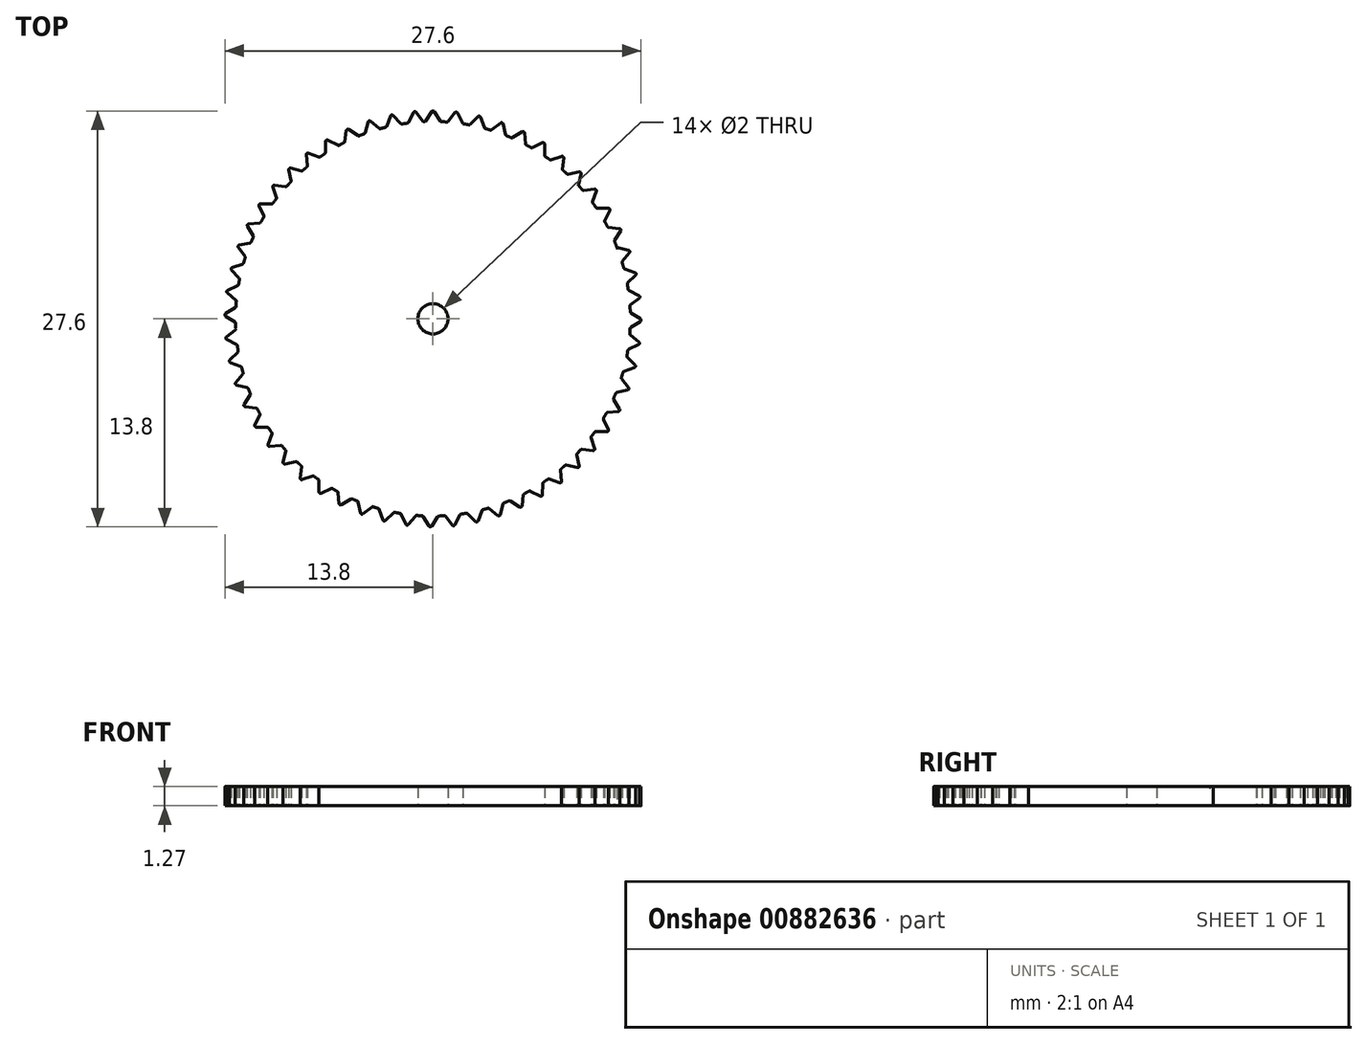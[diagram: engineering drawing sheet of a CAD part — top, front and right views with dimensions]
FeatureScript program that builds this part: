
annotation { "Feature Type Name" : "Feature", "Feature Type Description" : "" }
export const myFeature = defineFeature(function(context is Context, id is Id, definition is map)
    precondition{}
    {
        {
            var Q0;
            Q0=qCreatedBy(makeId("Top.planeOp"),FACE);
            var sketch = newSketch(context, id + "F0", { "sketchPlane" : qUnion([Q0])});
            skArc(sketch, "E0", {"start": v(-0.5, 13.09) * mm, "mid": v(0, -13.1) * mm, "end": v(0.5, 13.09) * mm});
            skLineSegment(sketch, "E1", {"start": v(-0.5, 13.09) * mm, "end": v(0, 13.9) * mm});
            skLineSegment(sketch, "E2", {"start": v(0, 13.9) * mm, "end": v(0.5, 13.09) * mm});
            skCircle(sketch, "E3", {"center": v(0, 0) * mm, "radius": 1 * mm});
            skLineSegment(sketch, "E4", {"start": v(-0.5, 13.09) * mm, "end": v(0.5, 13.09) * mm});
            skLineSegment(sketch, "E5.1.0", {"start": v(0.97, 13.06) * mm, "end": v(1.56, 13.8) * mm});
            skLineSegment(sketch, "E5.1.1", {"start": v(1.56, 13.8) * mm, "end": v(1.98, 12.95) * mm});
            skLineSegment(sketch, "E5.2.0", {"start": v(2.43, 12.87) * mm, "end": v(3.1, 13.54) * mm});
            skLineSegment(sketch, "E5.2.1", {"start": v(3.1, 13.54) * mm, "end": v(3.42, 12.64) * mm});
            skLineSegment(sketch, "E5.3.0", {"start": v(3.86, 12.52) * mm, "end": v(4.6, 13.1) * mm});
            skLineSegment(sketch, "E5.3.1", {"start": v(4.6, 13.1) * mm, "end": v(4.82, 12.18) * mm});
            skLineSegment(sketch, "E5.4.0", {"start": v(5.24, 12) * mm, "end": v(6.05, 12.5) * mm});
            skLineSegment(sketch, "E5.4.1", {"start": v(6.05, 12.5) * mm, "end": v(6.16, 11.56) * mm});
            skLineSegment(sketch, "E5.5.0", {"start": v(6.56, 11.34) * mm, "end": v(7.42, 11.75) * mm});
            skLineSegment(sketch, "E5.5.1", {"start": v(7.42, 11.75) * mm, "end": v(7.42, 10.8) * mm});
            skLineSegment(sketch, "E5.6.0", {"start": v(7.8, 10.53) * mm, "end": v(8.7, 10.84) * mm});
            skLineSegment(sketch, "E5.6.1", {"start": v(8.7, 10.84) * mm, "end": v(8.58, 9.9) * mm});
            skLineSegment(sketch, "E5.7.0", {"start": v(8.93, 9.58) * mm, "end": v(9.85, 9.8) * mm});
            skLineSegment(sketch, "E5.7.1", {"start": v(9.85, 9.8) * mm, "end": v(9.64, 8.86) * mm});
            skLineSegment(sketch, "E5.8.0", {"start": v(9.95, 8.52) * mm, "end": v(10.9, 8.62) * mm});
            skLineSegment(sketch, "E5.8.1", {"start": v(10.9, 8.62) * mm, "end": v(10.58, 7.72) * mm});
            skLineSegment(sketch, "E5.9.0", {"start": v(10.84, 7.35) * mm, "end": v(11.8, 7.34) * mm});
            skLineSegment(sketch, "E5.9.1", {"start": v(11.8, 7.34) * mm, "end": v(11.38, 6.49) * mm});
            skLineSegment(sketch, "E5.10.0", {"start": v(11.6, 6.08) * mm, "end": v(12.54, 5.97) * mm});
            skLineSegment(sketch, "E5.10.1", {"start": v(12.54, 5.97) * mm, "end": v(12.03, 5.17) * mm});
            skLineSegment(sketch, "E5.11.0", {"start": v(12.2, 4.74) * mm, "end": v(13.13, 4.52) * mm});
            skLineSegment(sketch, "E5.11.1", {"start": v(13.13, 4.52) * mm, "end": v(12.54, 3.78) * mm});
            skLineSegment(sketch, "E5.12.0", {"start": v(12.66, 3.34) * mm, "end": v(13.56, 3.02) * mm});
            skLineSegment(sketch, "E5.12.1", {"start": v(13.56, 3.02) * mm, "end": v(12.88, 2.35) * mm});
            skLineSegment(sketch, "E5.13.0", {"start": v(12.96, 1.9) * mm, "end": v(13.81, 1.47) * mm});
            skLineSegment(sketch, "E5.13.1", {"start": v(13.81, 1.47) * mm, "end": v(13.07, 0.88) * mm});
            skLineSegment(sketch, "E5.14.0", {"start": v(13.09, 0.42) * mm, "end": v(13.9, -0.09) * mm});
            skLineSegment(sketch, "E5.14.1", {"start": v(13.9, -0.09) * mm, "end": v(13.08, -0.6) * mm});
            skLineSegment(sketch, "E5.15.0", {"start": v(13.05, -1.05) * mm, "end": v(13.8, -1.65) * mm});
            skLineSegment(sketch, "E5.15.1", {"start": v(13.8, -1.65) * mm, "end": v(12.93, -2.06) * mm});
            skLineSegment(sketch, "E5.16.0", {"start": v(12.85, -2.51) * mm, "end": v(13.52, -3.19) * mm});
            skLineSegment(sketch, "E5.16.1", {"start": v(13.52, -3.19) * mm, "end": v(12.62, -3.5) * mm});
            skLineSegment(sketch, "E5.17.0", {"start": v(12.5, -3.94) * mm, "end": v(13.08, -4.69) * mm});
            skLineSegment(sketch, "E5.17.1", {"start": v(13.08, -4.69) * mm, "end": v(12.15, -4.9) * mm});
            skLineSegment(sketch, "E5.18.0", {"start": v(11.97, -5.32) * mm, "end": v(12.47, -6.13) * mm});
            skLineSegment(sketch, "E5.18.1", {"start": v(12.47, -6.13) * mm, "end": v(11.52, -6.23) * mm});
            skLineSegment(sketch, "E5.19.0", {"start": v(11.3, -6.63) * mm, "end": v(11.7, -7.5) * mm});
            skLineSegment(sketch, "E5.19.1", {"start": v(11.7, -7.5) * mm, "end": v(10.75, -7.49) * mm});
            skLineSegment(sketch, "E5.20.0", {"start": v(10.48, -7.86) * mm, "end": v(10.78, -8.76) * mm});
            skLineSegment(sketch, "E5.20.1", {"start": v(10.78, -8.76) * mm, "end": v(9.84, -8.65) * mm});
            skLineSegment(sketch, "E5.21.0", {"start": v(9.53, -8.99) * mm, "end": v(9.73, -9.92) * mm});
            skLineSegment(sketch, "E5.21.1", {"start": v(9.73, -9.92) * mm, "end": v(8.8, -9.7) * mm});
            skLineSegment(sketch, "E5.22.0", {"start": v(8.46, -10) * mm, "end": v(8.55, -10.95) * mm});
            skLineSegment(sketch, "E5.22.1", {"start": v(8.55, -10.95) * mm, "end": v(7.66, -10.63) * mm});
            skLineSegment(sketch, "E5.23.0", {"start": v(7.28, -10.89) * mm, "end": v(7.27, -11.84) * mm});
            skLineSegment(sketch, "E5.23.1", {"start": v(7.27, -11.84) * mm, "end": v(6.41, -11.42) * mm});
            skLineSegment(sketch, "E5.24.0", {"start": v(6, -11.64) * mm, "end": v(5.9, -12.58) * mm});
            skLineSegment(sketch, "E5.24.1", {"start": v(5.9, -12.58) * mm, "end": v(5.09, -12.07) * mm});
            skLineSegment(sketch, "E5.25.0", {"start": v(4.66, -12.24) * mm, "end": v(4.44, -13.16) * mm});
            skLineSegment(sketch, "E5.25.1", {"start": v(4.44, -13.16) * mm, "end": v(3.7, -12.56) * mm});
            skLineSegment(sketch, "E5.26.0", {"start": v(3.26, -12.69) * mm, "end": v(2.93, -13.58) * mm});
            skLineSegment(sketch, "E5.26.1", {"start": v(2.93, -13.58) * mm, "end": v(2.26, -12.9) * mm});
            skLineSegment(sketch, "E5.27.0", {"start": v(1.81, -12.97) * mm, "end": v(1.39, -13.82) * mm});
            skLineSegment(sketch, "E5.27.1", {"start": v(1.39, -13.82) * mm, "end": v(0.8, -13.07) * mm});
            skLineSegment(sketch, "E5.28.0", {"start": v(0.34, -13.1) * mm, "end": v(-0.18, -13.9) * mm});
            skLineSegment(sketch, "E5.28.1", {"start": v(-0.18, -13.9) * mm, "end": v(-0.67, -13.08) * mm});
            skLineSegment(sketch, "E5.29.0", {"start": v(-1.13, -13.05) * mm, "end": v(-1.74, -13.78) * mm});
            skLineSegment(sketch, "E5.29.1", {"start": v(-1.74, -13.78) * mm, "end": v(-2.14, -12.92) * mm});
            skLineSegment(sketch, "E5.30.0", {"start": v(-2.6, -12.84) * mm, "end": v(-3.28, -13.5) * mm});
            skLineSegment(sketch, "E5.30.1", {"start": v(-3.28, -13.5) * mm, "end": v(-3.58, -12.6) * mm});
            skLineSegment(sketch, "E5.31.0", {"start": v(-4.02, -12.47) * mm, "end": v(-4.77, -13.05) * mm});
            skLineSegment(sketch, "E5.31.1", {"start": v(-4.77, -13.05) * mm, "end": v(-4.97, -12.12) * mm});
            skLineSegment(sketch, "E5.32.0", {"start": v(-5.4, -11.93) * mm, "end": v(-6.2, -12.43) * mm});
            skLineSegment(sketch, "E5.32.1", {"start": v(-6.2, -12.43) * mm, "end": v(-6.3, -11.48) * mm});
            skLineSegment(sketch, "E5.33.0", {"start": v(-6.7, -11.25) * mm, "end": v(-7.57, -11.65) * mm});
            skLineSegment(sketch, "E5.33.1", {"start": v(-7.57, -11.65) * mm, "end": v(-7.55, -10.7) * mm});
            skLineSegment(sketch, "E5.34.0", {"start": v(-7.92, -10.43) * mm, "end": v(-8.83, -10.73) * mm});
            skLineSegment(sketch, "E5.34.1", {"start": v(-8.83, -10.73) * mm, "end": v(-8.7, -9.78) * mm});
            skLineSegment(sketch, "E5.35.0", {"start": v(-9.05, -9.47) * mm, "end": v(-9.98, -9.67) * mm});
            skLineSegment(sketch, "E5.35.1", {"start": v(-9.98, -9.67) * mm, "end": v(-9.75, -8.74) * mm});
            skLineSegment(sketch, "E5.36.0", {"start": v(-10.05, -8.4) * mm, "end": v(-11, -8.48) * mm});
            skLineSegment(sketch, "E5.36.1", {"start": v(-11, -8.48) * mm, "end": v(-10.67, -7.59) * mm});
            skLineSegment(sketch, "E5.37.0", {"start": v(-10.93, -7.21) * mm, "end": v(-11.88, -7.2) * mm});
            skLineSegment(sketch, "E5.37.1", {"start": v(-11.88, -7.2) * mm, "end": v(-11.46, -6.34) * mm});
            skLineSegment(sketch, "E5.38.0", {"start": v(-11.67, -5.94) * mm, "end": v(-12.62, -5.81) * mm});
            skLineSegment(sketch, "E5.38.1", {"start": v(-12.62, -5.81) * mm, "end": v(-12.1, -5.01) * mm});
            skLineSegment(sketch, "E5.39.0", {"start": v(-12.27, -4.59) * mm, "end": v(-13.2, -4.36) * mm});
            skLineSegment(sketch, "E5.39.1", {"start": v(-13.2, -4.36) * mm, "end": v(-12.59, -3.62) * mm});
            skLineSegment(sketch, "E5.40.0", {"start": v(-12.7, -3.18) * mm, "end": v(-13.6, -2.85) * mm});
            skLineSegment(sketch, "E5.40.1", {"start": v(-13.6, -2.85) * mm, "end": v(-12.91, -2.18) * mm});
            skLineSegment(sketch, "E5.41.0", {"start": v(-12.98, -1.73) * mm, "end": v(-13.83, -1.3) * mm});
            skLineSegment(sketch, "E5.41.1", {"start": v(-13.83, -1.3) * mm, "end": v(-13.08, -0.72) * mm});
            skLineSegment(sketch, "E5.42.0", {"start": v(-13.1, -0.26) * mm, "end": v(-13.89, 0.26) * mm});
            skLineSegment(sketch, "E5.42.1", {"start": v(-13.89, 0.26) * mm, "end": v(-13.07, 0.76) * mm});
            skLineSegment(sketch, "E5.43.0", {"start": v(-13.04, 1.21) * mm, "end": v(-13.77, 1.82) * mm});
            skLineSegment(sketch, "E5.43.1", {"start": v(-13.77, 1.82) * mm, "end": v(-12.9, 2.22) * mm});
            skLineSegment(sketch, "E5.44.0", {"start": v(-12.82, 2.67) * mm, "end": v(-13.48, 3.36) * mm});
            skLineSegment(sketch, "E5.44.1", {"start": v(-13.48, 3.36) * mm, "end": v(-12.58, 3.66) * mm});
            skLineSegment(sketch, "E5.45.0", {"start": v(-12.44, 4.1) * mm, "end": v(-13.02, 4.85) * mm});
            skLineSegment(sketch, "E5.45.1", {"start": v(-13.02, 4.85) * mm, "end": v(-12.08, 5.05) * mm});
            skLineSegment(sketch, "E5.46.0", {"start": v(-11.9, 5.47) * mm, "end": v(-12.39, 6.29) * mm});
            skLineSegment(sketch, "E5.46.1", {"start": v(-12.39, 6.29) * mm, "end": v(-11.44, 6.38) * mm});
            skLineSegment(sketch, "E5.47.0", {"start": v(-11.2, 6.77) * mm, "end": v(-11.6, 7.64) * mm});
            skLineSegment(sketch, "E5.47.1", {"start": v(-11.6, 7.64) * mm, "end": v(-10.65, 7.62) * mm});
            skLineSegment(sketch, "E5.48.0", {"start": v(-10.38, 8) * mm, "end": v(-10.67, 8.9) * mm});
            skLineSegment(sketch, "E5.48.1", {"start": v(-10.67, 8.9) * mm, "end": v(-9.73, 8.77) * mm});
            skLineSegment(sketch, "E5.49.0", {"start": v(-9.41, 9.1) * mm, "end": v(-9.6, 10.04) * mm});
            skLineSegment(sketch, "E5.49.1", {"start": v(-9.6, 10.04) * mm, "end": v(-8.68, 9.8) * mm});
            skLineSegment(sketch, "E5.50.0", {"start": v(-8.33, 10.1) * mm, "end": v(-8.41, 11.05) * mm});
            skLineSegment(sketch, "E5.50.1", {"start": v(-8.41, 11.05) * mm, "end": v(-7.52, 10.72) * mm});
            skLineSegment(sketch, "E5.51.0", {"start": v(-7.14, 10.98) * mm, "end": v(-7.12, 11.93) * mm});
            skLineSegment(sketch, "E5.51.1", {"start": v(-7.12, 11.93) * mm, "end": v(-6.27, 11.5) * mm});
            skLineSegment(sketch, "E5.52.0", {"start": v(-5.86, 11.71) * mm, "end": v(-5.73, 12.65) * mm});
            skLineSegment(sketch, "E5.52.1", {"start": v(-5.73, 12.65) * mm, "end": v(-4.94, 12.13) * mm});
            skLineSegment(sketch, "E5.53.0", {"start": v(-4.5, 12.3) * mm, "end": v(-4.27, 13.22) * mm});
            skLineSegment(sketch, "E5.53.1", {"start": v(-4.27, 13.22) * mm, "end": v(-3.54, 12.6) * mm});
            skLineSegment(sketch, "E5.54.0", {"start": v(-3.1, 12.73) * mm, "end": v(-2.76, 13.61) * mm});
            skLineSegment(sketch, "E5.54.1", {"start": v(-2.76, 13.61) * mm, "end": v(-2.1, 12.93) * mm});
            skLineSegment(sketch, "E5.55.0", {"start": v(-1.65, 13) * mm, "end": v(-1.21, 13.84) * mm});
            skLineSegment(sketch, "E5.55.1", {"start": v(-1.21, 13.84) * mm, "end": v(-0.63, 13.08) * mm});
            skLineSegment(sketch, "E5.anchor1", {"start": v(0, 0) * mm, "end": v(-0.5, 13.09) * mm, "construction": true});
            skLineSegment(sketch, "E5.anchor2", {"start": v(0, 0) * mm, "end": v(-1.65, 13) * mm, "construction": true});
            skSolve(sketch);
        }
        {
            var Q0;
            {var subQ0=sQuery(id+"F0.wireOp",EDGE,"E0");var subQ1=makeQuery(id+"F0.imprint","INTERSECT",VERTEX,{"derivedFrom":[subQ0,sQuery(id+"F0.wireOp",EDGE,"E2")]});Q0=makeQuery(id+"F0.imprint","IMPRINT",FACE,{"disambiguationData":[TD([[makeQuery(id+"F0.imprint","IMPRINT",EDGE,{"disambiguationData":[TD([[subQ1,-1.0]])],"derivedFrom":subQ0}),1.0]])]});}
            var Q1;
            {var subQ0=sQuery(id+"F0.wireOp",EDGE,"E2");Q1=makeQuery(id+"F0.imprint","IMPRINT",FACE,{"disambiguationData":[TD([[makeQuery(id+"F0.imprint","IMPRINT",EDGE,{"derivedFrom":subQ0}),-1.0]])]});}
            var Q2;
            {var subQ0=sQuery(id+"F0.wireOp",EDGE,"E1");Q2=makeQuery(id+"F0.imprint","IMPRINT",FACE,{"disambiguationData":[TD([[makeQuery(id+"F0.imprint","IMPRINT",EDGE,{"derivedFrom":subQ0}),-1.0]])]});}
            var Q3;
            {var subQ0=sQuery(id+"F0.wireOp",EDGE,"E5.55.0");Q3=makeQuery(id+"F0.imprint","IMPRINT",FACE,{"disambiguationData":[TD([[makeQuery(id+"F0.imprint","IMPRINT",EDGE,{"derivedFrom":subQ0}),-1.0]])]});}
            var Q4;
            {var subQ0=sQuery(id+"F0.wireOp",EDGE,"E5.54.0");Q4=makeQuery(id+"F0.imprint","IMPRINT",FACE,{"disambiguationData":[TD([[makeQuery(id+"F0.imprint","IMPRINT",EDGE,{"derivedFrom":subQ0}),-1.0]])]});}
            var Q5;
            {var subQ0=sQuery(id+"F0.wireOp",EDGE,"E5.53.0");Q5=makeQuery(id+"F0.imprint","IMPRINT",FACE,{"disambiguationData":[TD([[makeQuery(id+"F0.imprint","IMPRINT",EDGE,{"derivedFrom":subQ0}),-1.0]])]});}
            var Q6;
            {var subQ0=sQuery(id+"F0.wireOp",EDGE,"E5.52.0");Q6=makeQuery(id+"F0.imprint","IMPRINT",FACE,{"disambiguationData":[TD([[makeQuery(id+"F0.imprint","IMPRINT",EDGE,{"derivedFrom":subQ0}),-1.0]])]});}
            var Q7;
            {var subQ0=sQuery(id+"F0.wireOp",EDGE,"E5.51.0");Q7=makeQuery(id+"F0.imprint","IMPRINT",FACE,{"disambiguationData":[TD([[makeQuery(id+"F0.imprint","IMPRINT",EDGE,{"derivedFrom":subQ0}),-1.0]])]});}
            var Q8;
            {var subQ0=sQuery(id+"F0.wireOp",EDGE,"E5.50.0");Q8=makeQuery(id+"F0.imprint","IMPRINT",FACE,{"disambiguationData":[TD([[makeQuery(id+"F0.imprint","IMPRINT",EDGE,{"derivedFrom":subQ0}),-1.0]])]});}
            var Q9;
            {var subQ0=sQuery(id+"F0.wireOp",EDGE,"E5.49.0");Q9=makeQuery(id+"F0.imprint","IMPRINT",FACE,{"disambiguationData":[TD([[makeQuery(id+"F0.imprint","IMPRINT",EDGE,{"derivedFrom":subQ0}),-1.0]])]});}
            var Q10;
            {var subQ0=sQuery(id+"F0.wireOp",EDGE,"E5.48.0");Q10=makeQuery(id+"F0.imprint","IMPRINT",FACE,{"disambiguationData":[TD([[makeQuery(id+"F0.imprint","IMPRINT",EDGE,{"derivedFrom":subQ0}),-1.0]])]});}
            var Q11;
            {var subQ0=sQuery(id+"F0.wireOp",EDGE,"E5.47.0");Q11=makeQuery(id+"F0.imprint","IMPRINT",FACE,{"disambiguationData":[TD([[makeQuery(id+"F0.imprint","IMPRINT",EDGE,{"derivedFrom":subQ0}),-1.0]])]});}
            var Q12;
            {var subQ0=sQuery(id+"F0.wireOp",EDGE,"E5.46.0");Q12=makeQuery(id+"F0.imprint","IMPRINT",FACE,{"disambiguationData":[TD([[makeQuery(id+"F0.imprint","IMPRINT",EDGE,{"derivedFrom":subQ0}),-1.0]])]});}
            var Q13;
            {var subQ0=sQuery(id+"F0.wireOp",EDGE,"E5.45.0");Q13=makeQuery(id+"F0.imprint","IMPRINT",FACE,{"disambiguationData":[TD([[makeQuery(id+"F0.imprint","IMPRINT",EDGE,{"derivedFrom":subQ0}),-1.0]])]});}
            var Q14;
            {var subQ0=sQuery(id+"F0.wireOp",EDGE,"E5.44.0");Q14=makeQuery(id+"F0.imprint","IMPRINT",FACE,{"disambiguationData":[TD([[makeQuery(id+"F0.imprint","IMPRINT",EDGE,{"derivedFrom":subQ0}),-1.0]])]});}
            var Q15;
            {var subQ0=sQuery(id+"F0.wireOp",EDGE,"E5.42.0");Q15=makeQuery(id+"F0.imprint","IMPRINT",FACE,{"disambiguationData":[TD([[makeQuery(id+"F0.imprint","IMPRINT",EDGE,{"derivedFrom":subQ0}),-1.0]])]});}
            var Q16;
            {var subQ0=sQuery(id+"F0.wireOp",EDGE,"E5.43.0");Q16=makeQuery(id+"F0.imprint","IMPRINT",FACE,{"disambiguationData":[TD([[makeQuery(id+"F0.imprint","IMPRINT",EDGE,{"derivedFrom":subQ0}),-1.0]])]});}
            var Q17;
            {var subQ0=sQuery(id+"F0.wireOp",EDGE,"E5.41.0");Q17=makeQuery(id+"F0.imprint","IMPRINT",FACE,{"disambiguationData":[TD([[makeQuery(id+"F0.imprint","IMPRINT",EDGE,{"derivedFrom":subQ0}),-1.0]])]});}
            var Q18;
            {var subQ0=sQuery(id+"F0.wireOp",EDGE,"E5.40.0");Q18=makeQuery(id+"F0.imprint","IMPRINT",FACE,{"disambiguationData":[TD([[makeQuery(id+"F0.imprint","IMPRINT",EDGE,{"derivedFrom":subQ0}),-1.0]])]});}
            var Q19;
            {var subQ0=sQuery(id+"F0.wireOp",EDGE,"E5.39.0");Q19=makeQuery(id+"F0.imprint","IMPRINT",FACE,{"disambiguationData":[TD([[makeQuery(id+"F0.imprint","IMPRINT",EDGE,{"derivedFrom":subQ0}),-1.0]])]});}
            var Q20;
            {var subQ0=sQuery(id+"F0.wireOp",EDGE,"E5.38.0");Q20=makeQuery(id+"F0.imprint","IMPRINT",FACE,{"disambiguationData":[TD([[makeQuery(id+"F0.imprint","IMPRINT",EDGE,{"derivedFrom":subQ0}),-1.0]])]});}
            var Q21;
            {var subQ0=sQuery(id+"F0.wireOp",EDGE,"E5.37.0");Q21=makeQuery(id+"F0.imprint","IMPRINT",FACE,{"disambiguationData":[TD([[makeQuery(id+"F0.imprint","IMPRINT",EDGE,{"derivedFrom":subQ0}),-1.0]])]});}
            var Q22;
            {var subQ0=sQuery(id+"F0.wireOp",EDGE,"E5.36.0");Q22=makeQuery(id+"F0.imprint","IMPRINT",FACE,{"disambiguationData":[TD([[makeQuery(id+"F0.imprint","IMPRINT",EDGE,{"derivedFrom":subQ0}),-1.0]])]});}
            var Q23;
            {var subQ0=sQuery(id+"F0.wireOp",EDGE,"E5.35.0");Q23=makeQuery(id+"F0.imprint","IMPRINT",FACE,{"disambiguationData":[TD([[makeQuery(id+"F0.imprint","IMPRINT",EDGE,{"derivedFrom":subQ0}),-1.0]])]});}
            var Q24;
            {var subQ0=sQuery(id+"F0.wireOp",EDGE,"E5.34.0");Q24=makeQuery(id+"F0.imprint","IMPRINT",FACE,{"disambiguationData":[TD([[makeQuery(id+"F0.imprint","IMPRINT",EDGE,{"derivedFrom":subQ0}),-1.0]])]});}
            var Q25;
            {var subQ0=sQuery(id+"F0.wireOp",EDGE,"E5.33.0");Q25=makeQuery(id+"F0.imprint","IMPRINT",FACE,{"disambiguationData":[TD([[makeQuery(id+"F0.imprint","IMPRINT",EDGE,{"derivedFrom":subQ0}),-1.0]])]});}
            var Q26;
            {var subQ0=sQuery(id+"F0.wireOp",EDGE,"E5.32.0");Q26=makeQuery(id+"F0.imprint","IMPRINT",FACE,{"disambiguationData":[TD([[makeQuery(id+"F0.imprint","IMPRINT",EDGE,{"derivedFrom":subQ0}),-1.0]])]});}
            var Q27;
            {var subQ0=sQuery(id+"F0.wireOp",EDGE,"E5.31.0");Q27=makeQuery(id+"F0.imprint","IMPRINT",FACE,{"disambiguationData":[TD([[makeQuery(id+"F0.imprint","IMPRINT",EDGE,{"derivedFrom":subQ0}),-1.0]])]});}
            var Q28;
            {var subQ0=sQuery(id+"F0.wireOp",EDGE,"E5.30.0");Q28=makeQuery(id+"F0.imprint","IMPRINT",FACE,{"disambiguationData":[TD([[makeQuery(id+"F0.imprint","IMPRINT",EDGE,{"derivedFrom":subQ0}),-1.0]])]});}
            var Q29;
            {var subQ0=sQuery(id+"F0.wireOp",EDGE,"E5.29.0");Q29=makeQuery(id+"F0.imprint","IMPRINT",FACE,{"disambiguationData":[TD([[makeQuery(id+"F0.imprint","IMPRINT",EDGE,{"derivedFrom":subQ0}),-1.0]])]});}
            var Q30;
            {var subQ0=sQuery(id+"F0.wireOp",EDGE,"E5.28.0");Q30=makeQuery(id+"F0.imprint","IMPRINT",FACE,{"disambiguationData":[TD([[makeQuery(id+"F0.imprint","IMPRINT",EDGE,{"derivedFrom":subQ0}),-1.0]])]});}
            var Q31;
            {var subQ0=sQuery(id+"F0.wireOp",EDGE,"E5.27.0");Q31=makeQuery(id+"F0.imprint","IMPRINT",FACE,{"disambiguationData":[TD([[makeQuery(id+"F0.imprint","IMPRINT",EDGE,{"derivedFrom":subQ0}),-1.0]])]});}
            var Q32;
            {var subQ0=sQuery(id+"F0.wireOp",EDGE,"E5.26.0");Q32=makeQuery(id+"F0.imprint","IMPRINT",FACE,{"disambiguationData":[TD([[makeQuery(id+"F0.imprint","IMPRINT",EDGE,{"derivedFrom":subQ0}),-1.0]])]});}
            var Q33;
            {var subQ0=sQuery(id+"F0.wireOp",EDGE,"E5.25.0");Q33=makeQuery(id+"F0.imprint","IMPRINT",FACE,{"disambiguationData":[TD([[makeQuery(id+"F0.imprint","IMPRINT",EDGE,{"derivedFrom":subQ0}),-1.0]])]});}
            var Q34;
            {var subQ0=sQuery(id+"F0.wireOp",EDGE,"E5.24.0");Q34=makeQuery(id+"F0.imprint","IMPRINT",FACE,{"disambiguationData":[TD([[makeQuery(id+"F0.imprint","IMPRINT",EDGE,{"derivedFrom":subQ0}),-1.0]])]});}
            var Q35;
            {var subQ0=sQuery(id+"F0.wireOp",EDGE,"E5.23.0");Q35=makeQuery(id+"F0.imprint","IMPRINT",FACE,{"disambiguationData":[TD([[makeQuery(id+"F0.imprint","IMPRINT",EDGE,{"derivedFrom":subQ0}),-1.0]])]});}
            var Q36;
            {var subQ0=sQuery(id+"F0.wireOp",EDGE,"E5.21.0");Q36=makeQuery(id+"F0.imprint","IMPRINT",FACE,{"disambiguationData":[TD([[makeQuery(id+"F0.imprint","IMPRINT",EDGE,{"derivedFrom":subQ0}),-1.0]])]});}
            var Q37;
            {var subQ0=sQuery(id+"F0.wireOp",EDGE,"E5.20.0");Q37=makeQuery(id+"F0.imprint","IMPRINT",FACE,{"disambiguationData":[TD([[makeQuery(id+"F0.imprint","IMPRINT",EDGE,{"derivedFrom":subQ0}),-1.0]])]});}
            var Q38;
            {var subQ0=sQuery(id+"F0.wireOp",EDGE,"E5.19.0");Q38=makeQuery(id+"F0.imprint","IMPRINT",FACE,{"disambiguationData":[TD([[makeQuery(id+"F0.imprint","IMPRINT",EDGE,{"derivedFrom":subQ0}),-1.0]])]});}
            var Q39;
            {var subQ0=sQuery(id+"F0.wireOp",EDGE,"E5.18.0");Q39=makeQuery(id+"F0.imprint","IMPRINT",FACE,{"disambiguationData":[TD([[makeQuery(id+"F0.imprint","IMPRINT",EDGE,{"derivedFrom":subQ0}),-1.0]])]});}
            var Q40;
            {var subQ0=sQuery(id+"F0.wireOp",EDGE,"E5.22.0");Q40=makeQuery(id+"F0.imprint","IMPRINT",FACE,{"disambiguationData":[TD([[makeQuery(id+"F0.imprint","IMPRINT",EDGE,{"derivedFrom":subQ0}),-1.0]])]});}
            var Q41;
            {var subQ0=sQuery(id+"F0.wireOp",EDGE,"E5.17.0");Q41=makeQuery(id+"F0.imprint","IMPRINT",FACE,{"disambiguationData":[TD([[makeQuery(id+"F0.imprint","IMPRINT",EDGE,{"derivedFrom":subQ0}),-1.0]])]});}
            var Q42;
            {var subQ0=sQuery(id+"F0.wireOp",EDGE,"E5.16.0");Q42=makeQuery(id+"F0.imprint","IMPRINT",FACE,{"disambiguationData":[TD([[makeQuery(id+"F0.imprint","IMPRINT",EDGE,{"derivedFrom":subQ0}),-1.0]])]});}
            var Q43;
            {var subQ0=sQuery(id+"F0.wireOp",EDGE,"E5.14.0");Q43=makeQuery(id+"F0.imprint","IMPRINT",FACE,{"disambiguationData":[TD([[makeQuery(id+"F0.imprint","IMPRINT",EDGE,{"derivedFrom":subQ0}),-1.0]])]});}
            var Q44;
            {var subQ0=sQuery(id+"F0.wireOp",EDGE,"E5.15.0");Q44=makeQuery(id+"F0.imprint","IMPRINT",FACE,{"disambiguationData":[TD([[makeQuery(id+"F0.imprint","IMPRINT",EDGE,{"derivedFrom":subQ0}),-1.0]])]});}
            var Q45;
            Q45=makeQuery(id+"F0.imprint","IMPRINT",FACE,{"disambiguationData":[TD([[makeQuery(id+"F0.imprint","IMPRINT",EDGE,{"derivedFrom":sQuery(id+"F0.wireOp",EDGE,"E3")}),-1.0]])]});
            var Q46;
            {var subQ0=sQuery(id+"F0.wireOp",EDGE,"E5.13.0");Q46=makeQuery(id+"F0.imprint","IMPRINT",FACE,{"disambiguationData":[TD([[makeQuery(id+"F0.imprint","IMPRINT",EDGE,{"derivedFrom":subQ0}),-1.0]])]});}
            var Q47;
            {var subQ0=sQuery(id+"F0.wireOp",EDGE,"E5.12.0");Q47=makeQuery(id+"F0.imprint","IMPRINT",FACE,{"disambiguationData":[TD([[makeQuery(id+"F0.imprint","IMPRINT",EDGE,{"derivedFrom":subQ0}),-1.0]])]});}
            var Q48;
            {var subQ0=sQuery(id+"F0.wireOp",EDGE,"E5.11.0");Q48=makeQuery(id+"F0.imprint","IMPRINT",FACE,{"disambiguationData":[TD([[makeQuery(id+"F0.imprint","IMPRINT",EDGE,{"derivedFrom":subQ0}),-1.0]])]});}
            var Q49;
            {var subQ0=sQuery(id+"F0.wireOp",EDGE,"E5.8.0");Q49=makeQuery(id+"F0.imprint","IMPRINT",FACE,{"disambiguationData":[TD([[makeQuery(id+"F0.imprint","IMPRINT",EDGE,{"derivedFrom":subQ0}),-1.0]])]});}
            var Q50;
            {var subQ0=sQuery(id+"F0.wireOp",EDGE,"E5.7.0");Q50=makeQuery(id+"F0.imprint","IMPRINT",FACE,{"disambiguationData":[TD([[makeQuery(id+"F0.imprint","IMPRINT",EDGE,{"derivedFrom":subQ0}),-1.0]])]});}
            var Q51;
            {var subQ0=sQuery(id+"F0.wireOp",EDGE,"E5.6.0");Q51=makeQuery(id+"F0.imprint","IMPRINT",FACE,{"disambiguationData":[TD([[makeQuery(id+"F0.imprint","IMPRINT",EDGE,{"derivedFrom":subQ0}),-1.0]])]});}
            var Q52;
            {var subQ0=sQuery(id+"F0.wireOp",EDGE,"E5.10.0");Q52=makeQuery(id+"F0.imprint","IMPRINT",FACE,{"disambiguationData":[TD([[makeQuery(id+"F0.imprint","IMPRINT",EDGE,{"derivedFrom":subQ0}),-1.0]])]});}
            var Q53;
            {var subQ0=sQuery(id+"F0.wireOp",EDGE,"E5.9.0");Q53=makeQuery(id+"F0.imprint","IMPRINT",FACE,{"disambiguationData":[TD([[makeQuery(id+"F0.imprint","IMPRINT",EDGE,{"derivedFrom":subQ0}),-1.0]])]});}
            var Q54;
            {var subQ0=sQuery(id+"F0.wireOp",EDGE,"E5.5.0");Q54=makeQuery(id+"F0.imprint","IMPRINT",FACE,{"disambiguationData":[TD([[makeQuery(id+"F0.imprint","IMPRINT",EDGE,{"derivedFrom":subQ0}),-1.0]])]});}
            var Q55;
            {var subQ0=sQuery(id+"F0.wireOp",EDGE,"E5.3.0");Q55=makeQuery(id+"F0.imprint","IMPRINT",FACE,{"disambiguationData":[TD([[makeQuery(id+"F0.imprint","IMPRINT",EDGE,{"derivedFrom":subQ0}),-1.0]])]});}
            var Q56;
            {var subQ0=sQuery(id+"F0.wireOp",EDGE,"E5.2.0");Q56=makeQuery(id+"F0.imprint","IMPRINT",FACE,{"disambiguationData":[TD([[makeQuery(id+"F0.imprint","IMPRINT",EDGE,{"derivedFrom":subQ0}),-1.0]])]});}
            var Q57;
            {var subQ0=sQuery(id+"F0.wireOp",EDGE,"E5.1.0");Q57=makeQuery(id+"F0.imprint","IMPRINT",FACE,{"disambiguationData":[TD([[makeQuery(id+"F0.imprint","IMPRINT",EDGE,{"derivedFrom":subQ0}),-1.0]])]});}
            var Q58;
            {var subQ0=sQuery(id+"F0.wireOp",EDGE,"E5.4.0");Q58=makeQuery(id+"F0.imprint","IMPRINT",FACE,{"disambiguationData":[TD([[makeQuery(id+"F0.imprint","IMPRINT",EDGE,{"derivedFrom":subQ0}),-1.0]])]});}
            extrude(context, id + "F1", {"entities" : qUnion([Q0, Q1, Q2, Q3, Q4, Q5, Q6, Q7, Q8, Q9, Q10, Q11, Q12, Q13, Q14, Q15, Q16, Q17, Q18, Q19, Q20, Q21, Q22, Q23, Q24, Q25, Q26, Q27, Q28, Q29, Q30, Q31, Q32, Q33, Q34, Q35, Q36, Q37, Q38, Q39, Q40, Q41, Q42, Q43, Q44, Q45, Q46, Q47, Q48, Q49, Q50, Q51, Q52, Q53, Q54, Q55, Q56, Q57, Q58]), "depth" : 1.27 * mm, "offsetDistance" : 25.4 * mm});
        }
        {
            var Q0;
            Q0=makeQuery(id+"F1.opExtrude","SWEPT_EDGE",EDGE,{"disambiguationData":[OSD([sQuery(id+"F0.wireOp",EDGE,"hA7iAoV0-JRGM-B4cx-GfAK-cCa6ma2gju5E"),sQuery(id+"F0.wireOp",EDGE,"E1"),sQuery(id+"F0.wireOp",EDGE,"E2")])]});
            var Q1;
            Q1=makeQuery(id+"F1.opExtrude","SWEPT_EDGE",EDGE,{"disambiguationData":[OSD([sQuery(id+"F0.wireOp",EDGE,"E0"),sQuery(id+"F0.wireOp",EDGE,"E5.41.1")])]});
            var Q2;
            Q2=makeQuery(id+"F1.opExtrude","SWEPT_EDGE",EDGE,{"disambiguationData":[OSD([sQuery(id+"F0.wireOp",EDGE,"E0"),sQuery(id+"F0.wireOp",EDGE,"E5.42.0")])]});
            var Q3;
            Q3=makeQuery(id+"F1.opExtrude","SWEPT_EDGE",EDGE,{"disambiguationData":[OSD([sQuery(id+"F0.wireOp",EDGE,"E5.42.0"),sQuery(id+"F0.wireOp",EDGE,"E5.42.1")])]});
            var Q4;
            Q4=makeQuery(id+"F1.opExtrude","SWEPT_EDGE",EDGE,{"disambiguationData":[OSD([sQuery(id+"F0.wireOp",EDGE,"E0"),sQuery(id+"F0.wireOp",EDGE,"E5.42.1")])]});
            var Q5;
            Q5=makeQuery(id+"F1.opExtrude","SWEPT_EDGE",EDGE,{"disambiguationData":[OSD([sQuery(id+"F0.wireOp",EDGE,"E0"),sQuery(id+"F0.wireOp",EDGE,"E5.43.0")])]});
            var Q6;
            Q6=makeQuery(id+"F1.opExtrude","SWEPT_EDGE",EDGE,{"disambiguationData":[OSD([sQuery(id+"F0.wireOp",EDGE,"E5.43.0"),sQuery(id+"F0.wireOp",EDGE,"E5.43.1")])]});
            var Q7;
            Q7=makeQuery(id+"F1.opExtrude","SWEPT_EDGE",EDGE,{"disambiguationData":[OSD([sQuery(id+"F0.wireOp",EDGE,"E0"),sQuery(id+"F0.wireOp",EDGE,"E5.43.1")])]});
            var Q8;
            Q8=makeQuery(id+"F1.opExtrude","SWEPT_EDGE",EDGE,{"disambiguationData":[OSD([sQuery(id+"F0.wireOp",EDGE,"E0"),sQuery(id+"F0.wireOp",EDGE,"E5.44.0")])]});
            var Q9;
            Q9=makeQuery(id+"F1.opExtrude","SWEPT_EDGE",EDGE,{"disambiguationData":[OSD([sQuery(id+"F0.wireOp",EDGE,"E5.44.0"),sQuery(id+"F0.wireOp",EDGE,"E5.44.1")])]});
            var Q10;
            Q10=makeQuery(id+"F1.opExtrude","SWEPT_EDGE",EDGE,{"disambiguationData":[OSD([sQuery(id+"F0.wireOp",EDGE,"E0"),sQuery(id+"F0.wireOp",EDGE,"E5.44.1")])]});
            var Q11;
            Q11=makeQuery(id+"F1.opExtrude","SWEPT_EDGE",EDGE,{"disambiguationData":[OSD([sQuery(id+"F0.wireOp",EDGE,"E0"),sQuery(id+"F0.wireOp",EDGE,"E5.45.0")])]});
            var Q12;
            Q12=makeQuery(id+"F1.opExtrude","SWEPT_EDGE",EDGE,{"disambiguationData":[OSD([sQuery(id+"F0.wireOp",EDGE,"E5.45.0"),sQuery(id+"F0.wireOp",EDGE,"E5.45.1")])]});
            var Q13;
            Q13=makeQuery(id+"F1.opExtrude","SWEPT_EDGE",EDGE,{"disambiguationData":[OSD([sQuery(id+"F0.wireOp",EDGE,"E0"),sQuery(id+"F0.wireOp",EDGE,"E5.45.1")])]});
            var Q14;
            Q14=makeQuery(id+"F1.opExtrude","SWEPT_EDGE",EDGE,{"disambiguationData":[OSD([sQuery(id+"F0.wireOp",EDGE,"E0"),sQuery(id+"F0.wireOp",EDGE,"E5.46.0")])]});
            var Q15;
            Q15=makeQuery(id+"F1.opExtrude","SWEPT_EDGE",EDGE,{"disambiguationData":[OSD([sQuery(id+"F0.wireOp",EDGE,"E5.46.0"),sQuery(id+"F0.wireOp",EDGE,"E5.46.1")])]});
            var Q16;
            Q16=makeQuery(id+"F1.opExtrude","SWEPT_EDGE",EDGE,{"disambiguationData":[OSD([sQuery(id+"F0.wireOp",EDGE,"E0"),sQuery(id+"F0.wireOp",EDGE,"E5.46.1")])]});
            var Q17;
            Q17=makeQuery(id+"F1.opExtrude","SWEPT_EDGE",EDGE,{"disambiguationData":[OSD([sQuery(id+"F0.wireOp",EDGE,"E0"),sQuery(id+"F0.wireOp",EDGE,"E5.47.0")])]});
            var Q18;
            Q18=makeQuery(id+"F1.opExtrude","SWEPT_EDGE",EDGE,{"disambiguationData":[OSD([sQuery(id+"F0.wireOp",EDGE,"E5.47.0"),sQuery(id+"F0.wireOp",EDGE,"E5.47.1")])]});
            var Q19;
            Q19=makeQuery(id+"F1.opExtrude","SWEPT_EDGE",EDGE,{"disambiguationData":[OSD([sQuery(id+"F0.wireOp",EDGE,"E0"),sQuery(id+"F0.wireOp",EDGE,"E5.47.1")])]});
            var Q20;
            Q20=makeQuery(id+"F1.opExtrude","SWEPT_EDGE",EDGE,{"disambiguationData":[OSD([sQuery(id+"F0.wireOp",EDGE,"E5.48.0"),sQuery(id+"F0.wireOp",EDGE,"E5.48.1")])]});
            var Q21;
            Q21=makeQuery(id+"F1.opExtrude","SWEPT_EDGE",EDGE,{"disambiguationData":[OSD([sQuery(id+"F0.wireOp",EDGE,"E0"),sQuery(id+"F0.wireOp",EDGE,"E5.48.1")])]});
            var Q22;
            Q22=makeQuery(id+"F1.opExtrude","SWEPT_EDGE",EDGE,{"disambiguationData":[OSD([sQuery(id+"F0.wireOp",EDGE,"E5.49.0"),sQuery(id+"F0.wireOp",EDGE,"E5.49.1")])]});
            var Q23;
            Q23=makeQuery(id+"F1.opExtrude","SWEPT_EDGE",EDGE,{"disambiguationData":[OSD([sQuery(id+"F0.wireOp",EDGE,"E0"),sQuery(id+"F0.wireOp",EDGE,"E5.49.0")])]});
            var Q24;
            Q24=makeQuery(id+"F1.opExtrude","SWEPT_EDGE",EDGE,{"disambiguationData":[OSD([sQuery(id+"F0.wireOp",EDGE,"E0"),sQuery(id+"F0.wireOp",EDGE,"E5.49.1")])]});
            var Q25;
            Q25=makeQuery(id+"F1.opExtrude","SWEPT_EDGE",EDGE,{"disambiguationData":[OSD([sQuery(id+"F0.wireOp",EDGE,"E0"),sQuery(id+"F0.wireOp",EDGE,"E5.50.0")])]});
            var Q26;
            Q26=makeQuery(id+"F1.opExtrude","SWEPT_EDGE",EDGE,{"disambiguationData":[OSD([sQuery(id+"F0.wireOp",EDGE,"E5.50.0"),sQuery(id+"F0.wireOp",EDGE,"E5.50.1")])]});
            var Q27;
            Q27=makeQuery(id+"F1.opExtrude","SWEPT_EDGE",EDGE,{"disambiguationData":[OSD([sQuery(id+"F0.wireOp",EDGE,"E0"),sQuery(id+"F0.wireOp",EDGE,"E5.50.1")])]});
            var Q28;
            Q28=makeQuery(id+"F1.opExtrude","SWEPT_EDGE",EDGE,{"disambiguationData":[OSD([sQuery(id+"F0.wireOp",EDGE,"E0"),sQuery(id+"F0.wireOp",EDGE,"E5.51.0")])]});
            var Q29;
            Q29=makeQuery(id+"F1.opExtrude","SWEPT_EDGE",EDGE,{"disambiguationData":[OSD([sQuery(id+"F0.wireOp",EDGE,"E5.51.0"),sQuery(id+"F0.wireOp",EDGE,"E5.51.1")])]});
            var Q30;
            Q30=makeQuery(id+"F1.opExtrude","SWEPT_EDGE",EDGE,{"disambiguationData":[OSD([sQuery(id+"F0.wireOp",EDGE,"E0"),sQuery(id+"F0.wireOp",EDGE,"E5.51.1")])]});
            var Q31;
            Q31=makeQuery(id+"F1.opExtrude","SWEPT_EDGE",EDGE,{"disambiguationData":[OSD([sQuery(id+"F0.wireOp",EDGE,"E0"),sQuery(id+"F0.wireOp",EDGE,"E5.52.0")])]});
            var Q32;
            Q32=makeQuery(id+"F1.opExtrude","SWEPT_EDGE",EDGE,{"disambiguationData":[OSD([sQuery(id+"F0.wireOp",EDGE,"E5.52.0"),sQuery(id+"F0.wireOp",EDGE,"E5.52.1")])]});
            var Q33;
            Q33=makeQuery(id+"F1.opExtrude","SWEPT_EDGE",EDGE,{"disambiguationData":[OSD([sQuery(id+"F0.wireOp",EDGE,"E0"),sQuery(id+"F0.wireOp",EDGE,"E5.52.1")])]});
            var Q34;
            Q34=makeQuery(id+"F1.opExtrude","SWEPT_EDGE",EDGE,{"disambiguationData":[OSD([sQuery(id+"F0.wireOp",EDGE,"E0"),sQuery(id+"F0.wireOp",EDGE,"E5.53.0")])]});
            var Q35;
            Q35=makeQuery(id+"F1.opExtrude","SWEPT_EDGE",EDGE,{"disambiguationData":[OSD([sQuery(id+"F0.wireOp",EDGE,"E5.53.0"),sQuery(id+"F0.wireOp",EDGE,"E5.53.1")])]});
            var Q36;
            Q36=makeQuery(id+"F1.opExtrude","SWEPT_EDGE",EDGE,{"disambiguationData":[OSD([sQuery(id+"F0.wireOp",EDGE,"E0"),sQuery(id+"F0.wireOp",EDGE,"E5.53.1")])]});
            var Q37;
            Q37=makeQuery(id+"F1.opExtrude","SWEPT_EDGE",EDGE,{"disambiguationData":[OSD([sQuery(id+"F0.wireOp",EDGE,"E5.54.0"),sQuery(id+"F0.wireOp",EDGE,"E5.54.1")])]});
            var Q38;
            Q38=makeQuery(id+"F1.opExtrude","SWEPT_EDGE",EDGE,{"disambiguationData":[OSD([sQuery(id+"F0.wireOp",EDGE,"E0"),sQuery(id+"F0.wireOp",EDGE,"E5.54.1")])]});
            var Q39;
            Q39=makeQuery(id+"F1.opExtrude","SWEPT_EDGE",EDGE,{"disambiguationData":[OSD([sQuery(id+"F0.wireOp",EDGE,"E0"),sQuery(id+"F0.wireOp",EDGE,"E5.54.0")])]});
            var Q40;
            Q40=makeQuery(id+"F1.opExtrude","SWEPT_EDGE",EDGE,{"disambiguationData":[OSD([sQuery(id+"F0.wireOp",EDGE,"E0"),sQuery(id+"F0.wireOp",EDGE,"E5.55.0")])]});
            var Q41;
            Q41=makeQuery(id+"F1.opExtrude","SWEPT_EDGE",EDGE,{"disambiguationData":[OSD([sQuery(id+"F0.wireOp",EDGE,"E5.55.0"),sQuery(id+"F0.wireOp",EDGE,"E5.55.1")])]});
            var Q42;
            Q42=makeQuery(id+"F1.opExtrude","SWEPT_EDGE",EDGE,{"disambiguationData":[OSD([sQuery(id+"F0.wireOp",EDGE,"E0"),sQuery(id+"F0.wireOp",EDGE,"E5.55.1")])]});
            var Q43;
            Q43=makeQuery(id+"F1.opExtrude","SWEPT_EDGE",EDGE,{"disambiguationData":[OSD([sQuery(id+"F0.wireOp",EDGE,"E0"),sQuery(id+"F0.wireOp",EDGE,"E1"),sQuery(id+"F0.wireOp",EDGE,"E4")])]});
            var Q44;
            Q44=makeQuery(id+"F1.opExtrude","SWEPT_EDGE",EDGE,{"disambiguationData":[OSD([sQuery(id+"F0.wireOp",EDGE,"E0"),sQuery(id+"F0.wireOp",EDGE,"E2"),sQuery(id+"F0.wireOp",EDGE,"E4")])]});
            var Q45;
            Q45=makeQuery(id+"F1.opExtrude","SWEPT_EDGE",EDGE,{"disambiguationData":[OSD([sQuery(id+"F0.wireOp",EDGE,"E0"),sQuery(id+"F0.wireOp",EDGE,"E5.1.0")])]});
            var Q46;
            Q46=makeQuery(id+"F1.opExtrude","SWEPT_EDGE",EDGE,{"disambiguationData":[OSD([sQuery(id+"F0.wireOp",EDGE,"E5.1.0"),sQuery(id+"F0.wireOp",EDGE,"E5.1.1")])]});
            var Q47;
            Q47=makeQuery(id+"F1.opExtrude","SWEPT_EDGE",EDGE,{"disambiguationData":[OSD([sQuery(id+"F0.wireOp",EDGE,"E0"),sQuery(id+"F0.wireOp",EDGE,"E5.2.0")])]});
            var Q48;
            Q48=makeQuery(id+"F1.opExtrude","SWEPT_EDGE",EDGE,{"disambiguationData":[OSD([sQuery(id+"F0.wireOp",EDGE,"E5.2.0"),sQuery(id+"F0.wireOp",EDGE,"E5.2.1")])]});
            var Q49;
            Q49=makeQuery(id+"F1.opExtrude","SWEPT_EDGE",EDGE,{"disambiguationData":[OSD([sQuery(id+"F0.wireOp",EDGE,"E0"),sQuery(id+"F0.wireOp",EDGE,"E5.2.1")])]});
            var Q50;
            Q50=makeQuery(id+"F1.opExtrude","SWEPT_EDGE",EDGE,{"disambiguationData":[OSD([sQuery(id+"F0.wireOp",EDGE,"E0"),sQuery(id+"F0.wireOp",EDGE,"E5.3.0")])]});
            var Q51;
            Q51=makeQuery(id+"F1.opExtrude","SWEPT_EDGE",EDGE,{"disambiguationData":[OSD([sQuery(id+"F0.wireOp",EDGE,"E5.3.0"),sQuery(id+"F0.wireOp",EDGE,"E5.3.1")])]});
            var Q52;
            Q52=makeQuery(id+"F1.opExtrude","SWEPT_EDGE",EDGE,{"disambiguationData":[OSD([sQuery(id+"F0.wireOp",EDGE,"E0"),sQuery(id+"F0.wireOp",EDGE,"E5.3.1")])]});
            var Q53;
            Q53=makeQuery(id+"F1.opExtrude","SWEPT_EDGE",EDGE,{"disambiguationData":[OSD([sQuery(id+"F0.wireOp",EDGE,"E5.4.0"),sQuery(id+"F0.wireOp",EDGE,"E5.4.1")])]});
            var Q54;
            Q54=makeQuery(id+"F1.opExtrude","SWEPT_EDGE",EDGE,{"disambiguationData":[OSD([sQuery(id+"F0.wireOp",EDGE,"E0"),sQuery(id+"F0.wireOp",EDGE,"E5.4.1")])]});
            var Q55;
            Q55=makeQuery(id+"F1.opExtrude","SWEPT_EDGE",EDGE,{"disambiguationData":[OSD([sQuery(id+"F0.wireOp",EDGE,"E0"),sQuery(id+"F0.wireOp",EDGE,"E5.5.0")])]});
            var Q56;
            Q56=makeQuery(id+"F1.opExtrude","SWEPT_EDGE",EDGE,{"disambiguationData":[OSD([sQuery(id+"F0.wireOp",EDGE,"E5.5.0"),sQuery(id+"F0.wireOp",EDGE,"E5.5.1")])]});
            var Q57;
            Q57=makeQuery(id+"F1.opExtrude","SWEPT_EDGE",EDGE,{"disambiguationData":[OSD([sQuery(id+"F0.wireOp",EDGE,"E0"),sQuery(id+"F0.wireOp",EDGE,"E5.4.0")])]});
            var Q58;
            Q58=makeQuery(id+"F1.opExtrude","SWEPT_EDGE",EDGE,{"disambiguationData":[OSD([sQuery(id+"F0.wireOp",EDGE,"E0"),sQuery(id+"F0.wireOp",EDGE,"E5.5.1")])]});
            var Q59;
            Q59=makeQuery(id+"F1.opExtrude","SWEPT_EDGE",EDGE,{"disambiguationData":[OSD([sQuery(id+"F0.wireOp",EDGE,"E0"),sQuery(id+"F0.wireOp",EDGE,"E5.6.0")])]});
            var Q60;
            Q60=makeQuery(id+"F1.opExtrude","SWEPT_EDGE",EDGE,{"disambiguationData":[OSD([sQuery(id+"F0.wireOp",EDGE,"E5.6.0"),sQuery(id+"F0.wireOp",EDGE,"E5.6.1")])]});
            var Q61;
            Q61=makeQuery(id+"F1.opExtrude","SWEPT_EDGE",EDGE,{"disambiguationData":[OSD([sQuery(id+"F0.wireOp",EDGE,"E0"),sQuery(id+"F0.wireOp",EDGE,"E5.6.1")])]});
            var Q62;
            Q62=makeQuery(id+"F1.opExtrude","SWEPT_EDGE",EDGE,{"disambiguationData":[OSD([sQuery(id+"F0.wireOp",EDGE,"E0"),sQuery(id+"F0.wireOp",EDGE,"E5.7.0")])]});
            var Q63;
            Q63=makeQuery(id+"F1.opExtrude","SWEPT_EDGE",EDGE,{"disambiguationData":[OSD([sQuery(id+"F0.wireOp",EDGE,"E5.7.0"),sQuery(id+"F0.wireOp",EDGE,"E5.7.1")])]});
            var Q64;
            Q64=makeQuery(id+"F1.opExtrude","SWEPT_EDGE",EDGE,{"disambiguationData":[OSD([sQuery(id+"F0.wireOp",EDGE,"E0"),sQuery(id+"F0.wireOp",EDGE,"E5.7.1")])]});
            var Q65;
            Q65=makeQuery(id+"F1.opExtrude","SWEPT_EDGE",EDGE,{"disambiguationData":[OSD([sQuery(id+"F0.wireOp",EDGE,"E0"),sQuery(id+"F0.wireOp",EDGE,"E5.8.0")])]});
            var Q66;
            Q66=makeQuery(id+"F1.opExtrude","SWEPT_EDGE",EDGE,{"disambiguationData":[OSD([sQuery(id+"F0.wireOp",EDGE,"E5.8.0"),sQuery(id+"F0.wireOp",EDGE,"E5.8.1")])]});
            var Q67;
            Q67=makeQuery(id+"F1.opExtrude","SWEPT_EDGE",EDGE,{"disambiguationData":[OSD([sQuery(id+"F0.wireOp",EDGE,"E0"),sQuery(id+"F0.wireOp",EDGE,"E5.8.1")])]});
            var Q68;
            Q68=makeQuery(id+"F1.opExtrude","SWEPT_EDGE",EDGE,{"disambiguationData":[OSD([sQuery(id+"F0.wireOp",EDGE,"E0"),sQuery(id+"F0.wireOp",EDGE,"E5.9.0")])]});
            var Q69;
            Q69=makeQuery(id+"F1.opExtrude","SWEPT_EDGE",EDGE,{"disambiguationData":[OSD([sQuery(id+"F0.wireOp",EDGE,"E5.9.0"),sQuery(id+"F0.wireOp",EDGE,"E5.9.1")])]});
            var Q70;
            Q70=makeQuery(id+"F1.opExtrude","SWEPT_EDGE",EDGE,{"disambiguationData":[OSD([sQuery(id+"F0.wireOp",EDGE,"E0"),sQuery(id+"F0.wireOp",EDGE,"E5.9.1")])]});
            var Q71;
            Q71=makeQuery(id+"F1.opExtrude","SWEPT_EDGE",EDGE,{"disambiguationData":[OSD([sQuery(id+"F0.wireOp",EDGE,"E0"),sQuery(id+"F0.wireOp",EDGE,"E5.10.0")])]});
            var Q72;
            Q72=makeQuery(id+"F1.opExtrude","SWEPT_EDGE",EDGE,{"disambiguationData":[OSD([sQuery(id+"F0.wireOp",EDGE,"E5.10.0"),sQuery(id+"F0.wireOp",EDGE,"E5.10.1")])]});
            var Q73;
            Q73=makeQuery(id+"F1.opExtrude","SWEPT_EDGE",EDGE,{"disambiguationData":[OSD([sQuery(id+"F0.wireOp",EDGE,"E0"),sQuery(id+"F0.wireOp",EDGE,"E5.10.1")])]});
            var Q74;
            Q74=makeQuery(id+"F1.opExtrude","CAP_EDGE",EDGE,{"disambiguationData":[OSD([sQuery(id+"F0.wireOp",EDGE,"E5.11.0")])],"isStart":false});
            var Q75;
            Q75=makeQuery(id+"F1.opExtrude","SWEPT_EDGE",EDGE,{"disambiguationData":[OSD([sQuery(id+"F0.wireOp",EDGE,"E0"),sQuery(id+"F0.wireOp",EDGE,"E5.11.1")])]});
            var Q76;
            Q76=makeQuery(id+"F1.opExtrude","SWEPT_EDGE",EDGE,{"disambiguationData":[OSD([sQuery(id+"F0.wireOp",EDGE,"E5.11.0"),sQuery(id+"F0.wireOp",EDGE,"E5.11.1")])]});
            var Q77;
            Q77=makeQuery(id+"F1.opExtrude","SWEPT_EDGE",EDGE,{"disambiguationData":[OSD([sQuery(id+"F0.wireOp",EDGE,"E0"),sQuery(id+"F0.wireOp",EDGE,"E5.12.0")])]});
            var Q78;
            Q78=makeQuery(id+"F1.opExtrude","SWEPT_EDGE",EDGE,{"disambiguationData":[OSD([sQuery(id+"F0.wireOp",EDGE,"E5.12.0"),sQuery(id+"F0.wireOp",EDGE,"E5.12.1")])]});
            var Q79;
            Q79=makeQuery(id+"F1.opExtrude","SWEPT_EDGE",EDGE,{"disambiguationData":[OSD([sQuery(id+"F0.wireOp",EDGE,"E0"),sQuery(id+"F0.wireOp",EDGE,"E5.12.1")])]});
            var Q80;
            Q80=makeQuery(id+"F1.opExtrude","SWEPT_EDGE",EDGE,{"disambiguationData":[OSD([sQuery(id+"F0.wireOp",EDGE,"E0"),sQuery(id+"F0.wireOp",EDGE,"E5.13.0")])]});
            var Q81;
            Q81=makeQuery(id+"F1.opExtrude","SWEPT_EDGE",EDGE,{"disambiguationData":[OSD([sQuery(id+"F0.wireOp",EDGE,"E5.13.0"),sQuery(id+"F0.wireOp",EDGE,"E5.13.1")])]});
            var Q82;
            Q82=makeQuery(id+"F1.opExtrude","SWEPT_EDGE",EDGE,{"disambiguationData":[OSD([sQuery(id+"F0.wireOp",EDGE,"E0"),sQuery(id+"F0.wireOp",EDGE,"E5.13.1")])]});
            var Q83;
            Q83=makeQuery(id+"F1.opExtrude","SWEPT_EDGE",EDGE,{"disambiguationData":[OSD([sQuery(id+"F0.wireOp",EDGE,"E0"),sQuery(id+"F0.wireOp",EDGE,"E5.14.0")])]});
            var Q84;
            Q84=makeQuery(id+"F1.opExtrude","SWEPT_EDGE",EDGE,{"disambiguationData":[OSD([sQuery(id+"F0.wireOp",EDGE,"E5.14.0"),sQuery(id+"F0.wireOp",EDGE,"E5.14.1")])]});
            var Q85;
            Q85=makeQuery(id+"F1.opExtrude","SWEPT_EDGE",EDGE,{"disambiguationData":[OSD([sQuery(id+"F0.wireOp",EDGE,"E0"),sQuery(id+"F0.wireOp",EDGE,"E5.14.1")])]});
            var Q86;
            Q86=makeQuery(id+"F1.opExtrude","SWEPT_EDGE",EDGE,{"disambiguationData":[OSD([sQuery(id+"F0.wireOp",EDGE,"E0"),sQuery(id+"F0.wireOp",EDGE,"E5.15.0")])]});
            var Q87;
            Q87=makeQuery(id+"F1.opExtrude","SWEPT_EDGE",EDGE,{"disambiguationData":[OSD([sQuery(id+"F0.wireOp",EDGE,"E5.15.0"),sQuery(id+"F0.wireOp",EDGE,"E5.15.1")])]});
            var Q88;
            Q88=makeQuery(id+"F1.opExtrude","SWEPT_EDGE",EDGE,{"disambiguationData":[OSD([sQuery(id+"F0.wireOp",EDGE,"E0"),sQuery(id+"F0.wireOp",EDGE,"E5.15.1")])]});
            var Q89;
            Q89=makeQuery(id+"F1.opExtrude","SWEPT_EDGE",EDGE,{"disambiguationData":[OSD([sQuery(id+"F0.wireOp",EDGE,"E0"),sQuery(id+"F0.wireOp",EDGE,"E5.16.0")])]});
            var Q90;
            Q90=makeQuery(id+"F1.opExtrude","SWEPT_EDGE",EDGE,{"disambiguationData":[OSD([sQuery(id+"F0.wireOp",EDGE,"E5.16.0"),sQuery(id+"F0.wireOp",EDGE,"E5.16.1")])]});
            var Q91;
            Q91=makeQuery(id+"F1.opExtrude","SWEPT_EDGE",EDGE,{"disambiguationData":[OSD([sQuery(id+"F0.wireOp",EDGE,"E0"),sQuery(id+"F0.wireOp",EDGE,"E5.16.1")])]});
            var Q92;
            Q92=makeQuery(id+"F1.opExtrude","SWEPT_EDGE",EDGE,{"disambiguationData":[OSD([sQuery(id+"F0.wireOp",EDGE,"E0"),sQuery(id+"F0.wireOp",EDGE,"E5.17.0")])]});
            var Q93;
            Q93=makeQuery(id+"F1.opExtrude","SWEPT_EDGE",EDGE,{"disambiguationData":[OSD([sQuery(id+"F0.wireOp",EDGE,"E5.17.0"),sQuery(id+"F0.wireOp",EDGE,"E5.17.1")])]});
            var Q94;
            Q94=makeQuery(id+"F1.opExtrude","SWEPT_EDGE",EDGE,{"disambiguationData":[OSD([sQuery(id+"F0.wireOp",EDGE,"E0"),sQuery(id+"F0.wireOp",EDGE,"E5.17.1")])]});
            var Q95;
            Q95=makeQuery(id+"F1.opExtrude","SWEPT_EDGE",EDGE,{"disambiguationData":[OSD([sQuery(id+"F0.wireOp",EDGE,"E0"),sQuery(id+"F0.wireOp",EDGE,"E5.18.0")])]});
            var Q96;
            Q96=makeQuery(id+"F1.opExtrude","SWEPT_EDGE",EDGE,{"disambiguationData":[OSD([sQuery(id+"F0.wireOp",EDGE,"E5.18.0"),sQuery(id+"F0.wireOp",EDGE,"E5.18.1")])]});
            var Q97;
            Q97=makeQuery(id+"F1.opExtrude","SWEPT_EDGE",EDGE,{"disambiguationData":[OSD([sQuery(id+"F0.wireOp",EDGE,"E0"),sQuery(id+"F0.wireOp",EDGE,"E5.18.1")])]});
            var Q98;
            Q98=makeQuery(id+"F1.opExtrude","SWEPT_EDGE",EDGE,{"disambiguationData":[OSD([sQuery(id+"F0.wireOp",EDGE,"E0"),sQuery(id+"F0.wireOp",EDGE,"E5.19.0")])]});
            var Q99;
            Q99=makeQuery(id+"F1.opExtrude","SWEPT_EDGE",EDGE,{"disambiguationData":[OSD([sQuery(id+"F0.wireOp",EDGE,"E5.19.0"),sQuery(id+"F0.wireOp",EDGE,"E5.19.1")])]});
            var Q100;
            Q100=makeQuery(id+"F1.opExtrude","SWEPT_EDGE",EDGE,{"disambiguationData":[OSD([sQuery(id+"F0.wireOp",EDGE,"E0"),sQuery(id+"F0.wireOp",EDGE,"E5.19.1")])]});
            var Q101;
            Q101=makeQuery(id+"F1.opExtrude","SWEPT_EDGE",EDGE,{"disambiguationData":[OSD([sQuery(id+"F0.wireOp",EDGE,"E0"),sQuery(id+"F0.wireOp",EDGE,"E5.20.0")])]});
            var Q102;
            Q102=makeQuery(id+"F1.opExtrude","SWEPT_EDGE",EDGE,{"disambiguationData":[OSD([sQuery(id+"F0.wireOp",EDGE,"E5.20.0"),sQuery(id+"F0.wireOp",EDGE,"E5.20.1")])]});
            var Q103;
            Q103=makeQuery(id+"F1.opExtrude","SWEPT_EDGE",EDGE,{"disambiguationData":[OSD([sQuery(id+"F0.wireOp",EDGE,"E0"),sQuery(id+"F0.wireOp",EDGE,"E5.20.1")])]});
            var Q104;
            Q104=makeQuery(id+"F1.opExtrude","SWEPT_EDGE",EDGE,{"disambiguationData":[OSD([sQuery(id+"F0.wireOp",EDGE,"E0"),sQuery(id+"F0.wireOp",EDGE,"E5.21.0")])]});
            var Q105;
            Q105=makeQuery(id+"F1.opExtrude","SWEPT_EDGE",EDGE,{"disambiguationData":[OSD([sQuery(id+"F0.wireOp",EDGE,"E5.21.0"),sQuery(id+"F0.wireOp",EDGE,"E5.21.1")])]});
            var Q106;
            Q106=makeQuery(id+"F1.opExtrude","SWEPT_EDGE",EDGE,{"disambiguationData":[OSD([sQuery(id+"F0.wireOp",EDGE,"E0"),sQuery(id+"F0.wireOp",EDGE,"E5.21.1")])]});
            var Q107;
            Q107=makeQuery(id+"F1.opExtrude","SWEPT_EDGE",EDGE,{"disambiguationData":[OSD([sQuery(id+"F0.wireOp",EDGE,"E5.22.0"),sQuery(id+"F0.wireOp",EDGE,"E5.22.1")])]});
            var Q108;
            Q108=makeQuery(id+"F1.opExtrude","SWEPT_EDGE",EDGE,{"disambiguationData":[OSD([sQuery(id+"F0.wireOp",EDGE,"E0"),sQuery(id+"F0.wireOp",EDGE,"E5.22.0")])]});
            var Q109;
            Q109=makeQuery(id+"F1.opExtrude","SWEPT_EDGE",EDGE,{"disambiguationData":[OSD([sQuery(id+"F0.wireOp",EDGE,"E0"),sQuery(id+"F0.wireOp",EDGE,"E5.22.1")])]});
            var Q110;
            Q110=makeQuery(id+"F1.opExtrude","SWEPT_EDGE",EDGE,{"disambiguationData":[OSD([sQuery(id+"F0.wireOp",EDGE,"E0"),sQuery(id+"F0.wireOp",EDGE,"E5.23.0")])]});
            var Q111;
            Q111=makeQuery(id+"F1.opExtrude","SWEPT_EDGE",EDGE,{"disambiguationData":[OSD([sQuery(id+"F0.wireOp",EDGE,"E5.23.0"),sQuery(id+"F0.wireOp",EDGE,"E5.23.1")])]});
            var Q112;
            Q112=makeQuery(id+"F1.opExtrude","SWEPT_EDGE",EDGE,{"disambiguationData":[OSD([sQuery(id+"F0.wireOp",EDGE,"E0"),sQuery(id+"F0.wireOp",EDGE,"E5.23.1")])]});
            var Q113;
            Q113=makeQuery(id+"F1.opExtrude","SWEPT_EDGE",EDGE,{"disambiguationData":[OSD([sQuery(id+"F0.wireOp",EDGE,"E0"),sQuery(id+"F0.wireOp",EDGE,"E5.24.0")])]});
            var Q114;
            Q114=makeQuery(id+"F1.opExtrude","SWEPT_EDGE",EDGE,{"disambiguationData":[OSD([sQuery(id+"F0.wireOp",EDGE,"E5.24.0"),sQuery(id+"F0.wireOp",EDGE,"E5.24.1")])]});
            var Q115;
            Q115=makeQuery(id+"F1.opExtrude","SWEPT_EDGE",EDGE,{"disambiguationData":[OSD([sQuery(id+"F0.wireOp",EDGE,"E0"),sQuery(id+"F0.wireOp",EDGE,"E5.24.1")])]});
            var Q116;
            Q116=makeQuery(id+"F1.opExtrude","SWEPT_EDGE",EDGE,{"disambiguationData":[OSD([sQuery(id+"F0.wireOp",EDGE,"E0"),sQuery(id+"F0.wireOp",EDGE,"E5.25.0")])]});
            var Q117;
            Q117=makeQuery(id+"F1.opExtrude","SWEPT_EDGE",EDGE,{"disambiguationData":[OSD([sQuery(id+"F0.wireOp",EDGE,"E5.25.0"),sQuery(id+"F0.wireOp",EDGE,"E5.25.1")])]});
            var Q118;
            Q118=makeQuery(id+"F1.opExtrude","SWEPT_EDGE",EDGE,{"disambiguationData":[OSD([sQuery(id+"F0.wireOp",EDGE,"E0"),sQuery(id+"F0.wireOp",EDGE,"E5.25.1")])]});
            var Q119;
            Q119=makeQuery(id+"F1.opExtrude","SWEPT_EDGE",EDGE,{"disambiguationData":[OSD([sQuery(id+"F0.wireOp",EDGE,"E0"),sQuery(id+"F0.wireOp",EDGE,"E5.26.0")])]});
            var Q120;
            Q120=makeQuery(id+"F1.opExtrude","SWEPT_EDGE",EDGE,{"disambiguationData":[OSD([sQuery(id+"F0.wireOp",EDGE,"E5.26.0"),sQuery(id+"F0.wireOp",EDGE,"E5.26.1")])]});
            var Q121;
            Q121=makeQuery(id+"F1.opExtrude","SWEPT_EDGE",EDGE,{"disambiguationData":[OSD([sQuery(id+"F0.wireOp",EDGE,"E0"),sQuery(id+"F0.wireOp",EDGE,"E5.26.1")])]});
            var Q122;
            Q122=makeQuery(id+"F1.opExtrude","SWEPT_EDGE",EDGE,{"disambiguationData":[OSD([sQuery(id+"F0.wireOp",EDGE,"E0"),sQuery(id+"F0.wireOp",EDGE,"E5.27.0")])]});
            var Q123;
            Q123=makeQuery(id+"F1.opExtrude","SWEPT_EDGE",EDGE,{"disambiguationData":[OSD([sQuery(id+"F0.wireOp",EDGE,"E5.27.0"),sQuery(id+"F0.wireOp",EDGE,"E5.27.1")])]});
            var Q124;
            Q124=makeQuery(id+"F1.opExtrude","SWEPT_EDGE",EDGE,{"disambiguationData":[OSD([sQuery(id+"F0.wireOp",EDGE,"E0"),sQuery(id+"F0.wireOp",EDGE,"E5.27.1")])]});
            var Q125;
            Q125=makeQuery(id+"F1.opExtrude","SWEPT_EDGE",EDGE,{"disambiguationData":[OSD([sQuery(id+"F0.wireOp",EDGE,"E0"),sQuery(id+"F0.wireOp",EDGE,"E5.28.0")])]});
            var Q126;
            Q126=makeQuery(id+"F1.opExtrude","SWEPT_EDGE",EDGE,{"disambiguationData":[OSD([sQuery(id+"F0.wireOp",EDGE,"E5.28.0"),sQuery(id+"F0.wireOp",EDGE,"E5.28.1")])]});
            var Q127;
            Q127=makeQuery(id+"F1.opExtrude","SWEPT_EDGE",EDGE,{"disambiguationData":[OSD([sQuery(id+"F0.wireOp",EDGE,"E0"),sQuery(id+"F0.wireOp",EDGE,"E5.28.1")])]});
            var Q128;
            Q128=makeQuery(id+"F1.opExtrude","SWEPT_EDGE",EDGE,{"disambiguationData":[OSD([sQuery(id+"F0.wireOp",EDGE,"E0"),sQuery(id+"F0.wireOp",EDGE,"E5.29.0")])]});
            var Q129;
            Q129=makeQuery(id+"F1.opExtrude","SWEPT_EDGE",EDGE,{"disambiguationData":[OSD([sQuery(id+"F0.wireOp",EDGE,"E5.29.0"),sQuery(id+"F0.wireOp",EDGE,"E5.29.1")])]});
            var Q130;
            Q130=makeQuery(id+"F1.opExtrude","SWEPT_EDGE",EDGE,{"disambiguationData":[OSD([sQuery(id+"F0.wireOp",EDGE,"E0"),sQuery(id+"F0.wireOp",EDGE,"E5.29.1")])]});
            var Q131;
            Q131=makeQuery(id+"F1.opExtrude","SWEPT_EDGE",EDGE,{"disambiguationData":[OSD([sQuery(id+"F0.wireOp",EDGE,"E0"),sQuery(id+"F0.wireOp",EDGE,"E5.30.0")])]});
            var Q132;
            Q132=makeQuery(id+"F1.opExtrude","SWEPT_EDGE",EDGE,{"disambiguationData":[OSD([sQuery(id+"F0.wireOp",EDGE,"E5.30.0"),sQuery(id+"F0.wireOp",EDGE,"E5.30.1")])]});
            var Q133;
            Q133=makeQuery(id+"F1.opExtrude","SWEPT_EDGE",EDGE,{"disambiguationData":[OSD([sQuery(id+"F0.wireOp",EDGE,"E0"),sQuery(id+"F0.wireOp",EDGE,"E5.30.1")])]});
            var Q134;
            Q134=makeQuery(id+"F1.opExtrude","SWEPT_EDGE",EDGE,{"disambiguationData":[OSD([sQuery(id+"F0.wireOp",EDGE,"E0"),sQuery(id+"F0.wireOp",EDGE,"E5.31.0")])]});
            var Q135;
            Q135=makeQuery(id+"F1.opExtrude","SWEPT_EDGE",EDGE,{"disambiguationData":[OSD([sQuery(id+"F0.wireOp",EDGE,"E5.31.0"),sQuery(id+"F0.wireOp",EDGE,"E5.31.1")])]});
            var Q136;
            Q136=makeQuery(id+"F1.opExtrude","SWEPT_EDGE",EDGE,{"disambiguationData":[OSD([sQuery(id+"F0.wireOp",EDGE,"E0"),sQuery(id+"F0.wireOp",EDGE,"E5.31.1")])]});
            var Q137;
            Q137=makeQuery(id+"F1.opExtrude","SWEPT_EDGE",EDGE,{"disambiguationData":[OSD([sQuery(id+"F0.wireOp",EDGE,"E0"),sQuery(id+"F0.wireOp",EDGE,"E5.32.0")])]});
            var Q138;
            Q138=makeQuery(id+"F1.opExtrude","SWEPT_EDGE",EDGE,{"disambiguationData":[OSD([sQuery(id+"F0.wireOp",EDGE,"E5.32.0"),sQuery(id+"F0.wireOp",EDGE,"E5.32.1")])]});
            var Q139;
            Q139=makeQuery(id+"F1.opExtrude","SWEPT_EDGE",EDGE,{"disambiguationData":[OSD([sQuery(id+"F0.wireOp",EDGE,"E0"),sQuery(id+"F0.wireOp",EDGE,"E5.32.1")])]});
            var Q140;
            Q140=makeQuery(id+"F1.opExtrude","SWEPT_EDGE",EDGE,{"disambiguationData":[OSD([sQuery(id+"F0.wireOp",EDGE,"E0"),sQuery(id+"F0.wireOp",EDGE,"E5.33.0")])]});
            var Q141;
            Q141=makeQuery(id+"F1.opExtrude","SWEPT_EDGE",EDGE,{"disambiguationData":[OSD([sQuery(id+"F0.wireOp",EDGE,"E5.33.0"),sQuery(id+"F0.wireOp",EDGE,"E5.33.1")])]});
            var Q142;
            Q142=makeQuery(id+"F1.opExtrude","SWEPT_EDGE",EDGE,{"disambiguationData":[OSD([sQuery(id+"F0.wireOp",EDGE,"E0"),sQuery(id+"F0.wireOp",EDGE,"E5.33.1")])]});
            var Q143;
            Q143=makeQuery(id+"F1.opExtrude","SWEPT_EDGE",EDGE,{"disambiguationData":[OSD([sQuery(id+"F0.wireOp",EDGE,"E0"),sQuery(id+"F0.wireOp",EDGE,"E5.34.0")])]});
            var Q144;
            Q144=makeQuery(id+"F1.opExtrude","SWEPT_EDGE",EDGE,{"disambiguationData":[OSD([sQuery(id+"F0.wireOp",EDGE,"E5.34.0"),sQuery(id+"F0.wireOp",EDGE,"E5.34.1")])]});
            var Q145;
            Q145=makeQuery(id+"F1.opExtrude","SWEPT_EDGE",EDGE,{"disambiguationData":[OSD([sQuery(id+"F0.wireOp",EDGE,"E0"),sQuery(id+"F0.wireOp",EDGE,"E5.34.1")])]});
            var Q146;
            Q146=makeQuery(id+"F1.opExtrude","SWEPT_EDGE",EDGE,{"disambiguationData":[OSD([sQuery(id+"F0.wireOp",EDGE,"E0"),sQuery(id+"F0.wireOp",EDGE,"E5.35.0")])]});
            var Q147;
            Q147=makeQuery(id+"F1.opExtrude","SWEPT_EDGE",EDGE,{"disambiguationData":[OSD([sQuery(id+"F0.wireOp",EDGE,"E5.35.0"),sQuery(id+"F0.wireOp",EDGE,"E5.35.1")])]});
            var Q148;
            Q148=makeQuery(id+"F1.opExtrude","SWEPT_EDGE",EDGE,{"disambiguationData":[OSD([sQuery(id+"F0.wireOp",EDGE,"E0"),sQuery(id+"F0.wireOp",EDGE,"E5.35.1")])]});
            var Q149;
            Q149=makeQuery(id+"F1.opExtrude","SWEPT_EDGE",EDGE,{"disambiguationData":[OSD([sQuery(id+"F0.wireOp",EDGE,"E0"),sQuery(id+"F0.wireOp",EDGE,"E5.36.0")])]});
            var Q150;
            Q150=makeQuery(id+"F1.opExtrude","SWEPT_EDGE",EDGE,{"disambiguationData":[OSD([sQuery(id+"F0.wireOp",EDGE,"E5.36.0"),sQuery(id+"F0.wireOp",EDGE,"E5.36.1")])]});
            var Q151;
            Q151=makeQuery(id+"F1.opExtrude","SWEPT_EDGE",EDGE,{"disambiguationData":[OSD([sQuery(id+"F0.wireOp",EDGE,"E0"),sQuery(id+"F0.wireOp",EDGE,"E5.36.1")])]});
            var Q152;
            Q152=makeQuery(id+"F1.opExtrude","SWEPT_EDGE",EDGE,{"disambiguationData":[OSD([sQuery(id+"F0.wireOp",EDGE,"E0"),sQuery(id+"F0.wireOp",EDGE,"E5.37.0")])]});
            var Q153;
            Q153=makeQuery(id+"F1.opExtrude","SWEPT_EDGE",EDGE,{"disambiguationData":[OSD([sQuery(id+"F0.wireOp",EDGE,"E5.37.0"),sQuery(id+"F0.wireOp",EDGE,"E5.37.1")])]});
            var Q154;
            Q154=makeQuery(id+"F1.opExtrude","SWEPT_EDGE",EDGE,{"disambiguationData":[OSD([sQuery(id+"F0.wireOp",EDGE,"E0"),sQuery(id+"F0.wireOp",EDGE,"E5.37.1")])]});
            var Q155;
            Q155=makeQuery(id+"F1.opExtrude","SWEPT_EDGE",EDGE,{"disambiguationData":[OSD([sQuery(id+"F0.wireOp",EDGE,"E0"),sQuery(id+"F0.wireOp",EDGE,"E5.38.0")])]});
            var Q156;
            Q156=makeQuery(id+"F1.opExtrude","SWEPT_EDGE",EDGE,{"disambiguationData":[OSD([sQuery(id+"F0.wireOp",EDGE,"E5.38.0"),sQuery(id+"F0.wireOp",EDGE,"E5.38.1")])]});
            var Q157;
            Q157=makeQuery(id+"F1.opExtrude","SWEPT_EDGE",EDGE,{"disambiguationData":[OSD([sQuery(id+"F0.wireOp",EDGE,"E0"),sQuery(id+"F0.wireOp",EDGE,"E5.38.1")])]});
            var Q158;
            Q158=makeQuery(id+"F1.opExtrude","SWEPT_EDGE",EDGE,{"disambiguationData":[OSD([sQuery(id+"F0.wireOp",EDGE,"E0"),sQuery(id+"F0.wireOp",EDGE,"E5.39.0")])]});
            var Q159;
            Q159=makeQuery(id+"F1.opExtrude","SWEPT_EDGE",EDGE,{"disambiguationData":[OSD([sQuery(id+"F0.wireOp",EDGE,"E5.39.0"),sQuery(id+"F0.wireOp",EDGE,"E5.39.1")])]});
            var Q160;
            Q160=makeQuery(id+"F1.opExtrude","SWEPT_EDGE",EDGE,{"disambiguationData":[OSD([sQuery(id+"F0.wireOp",EDGE,"E0"),sQuery(id+"F0.wireOp",EDGE,"E5.39.1")])]});
            var Q161;
            Q161=makeQuery(id+"F1.opExtrude","SWEPT_EDGE",EDGE,{"disambiguationData":[OSD([sQuery(id+"F0.wireOp",EDGE,"E0"),sQuery(id+"F0.wireOp",EDGE,"E5.40.0")])]});
            var Q162;
            Q162=makeQuery(id+"F1.opExtrude","SWEPT_EDGE",EDGE,{"disambiguationData":[OSD([sQuery(id+"F0.wireOp",EDGE,"E5.40.0"),sQuery(id+"F0.wireOp",EDGE,"E5.40.1")])]});
            var Q163;
            Q163=makeQuery(id+"F1.opExtrude","SWEPT_EDGE",EDGE,{"disambiguationData":[OSD([sQuery(id+"F0.wireOp",EDGE,"E0"),sQuery(id+"F0.wireOp",EDGE,"E5.41.0")])]});
            var Q164;
            Q164=makeQuery(id+"F1.opExtrude","SWEPT_EDGE",EDGE,{"disambiguationData":[OSD([sQuery(id+"F0.wireOp",EDGE,"E5.41.0"),sQuery(id+"F0.wireOp",EDGE,"E5.41.1")])]});
            var Q165;
            Q165=makeQuery(id+"F1.opExtrude","SWEPT_EDGE",EDGE,{"disambiguationData":[OSD([sQuery(id+"F0.wireOp",EDGE,"E0"),sQuery(id+"F0.wireOp",EDGE,"E5.40.1")])]});
            fillet(context, id + "F2", {"entities" : qUnion([Q0, Q1, Q2, Q3, Q4, Q5, Q6, Q7, Q8, Q9, Q10, Q11, Q12, Q13, Q14, Q15, Q16, Q17, Q18, Q19, Q20, Q21, Q22, Q23, Q24, Q25, Q26, Q27, Q28, Q29, Q30, Q31, Q32, Q33, Q34, Q35, Q36, Q37, Q38, Q39, Q40, Q41, Q42, Q43, Q44, Q45, Q46, Q47, Q48, Q49, Q50, Q51, Q52, Q53, Q54, Q55, Q56, Q57, Q58, Q59, Q60, Q61, Q62, Q63, Q64, Q65, Q66, Q67, Q68, Q69, Q70, Q71, Q72, Q73, Q74, Q75, Q76, Q77, Q78, Q79, Q80, Q81, Q82, Q83, Q84, Q85, Q86, Q87, Q88, Q89, Q90, Q91, Q92, Q93, Q94, Q95, Q96, Q97, Q98, Q99, Q100, Q101, Q102, Q103, Q104, Q105, Q106, Q107, Q108, Q109, Q110, Q111, Q112, Q113, Q114, Q115, Q116, Q117, Q118, Q119, Q120, Q121, Q122, Q123, Q124, Q125, Q126, Q127, Q128, Q129, Q130, Q131, Q132, Q133, Q134, Q135, Q136, Q137, Q138, Q139, Q140, Q141, Q142, Q143, Q144, Q145, Q146, Q147, Q148, Q149, Q150, Q151, Q152, Q153, Q154, Q155, Q156, Q157, Q158, Q159, Q160, Q161, Q162, Q163, Q164, Q165]), "radius" : 0.1 * mm, "tangentPropagation" : true, "allowEdgeOverflow" : false});
        }
    });
